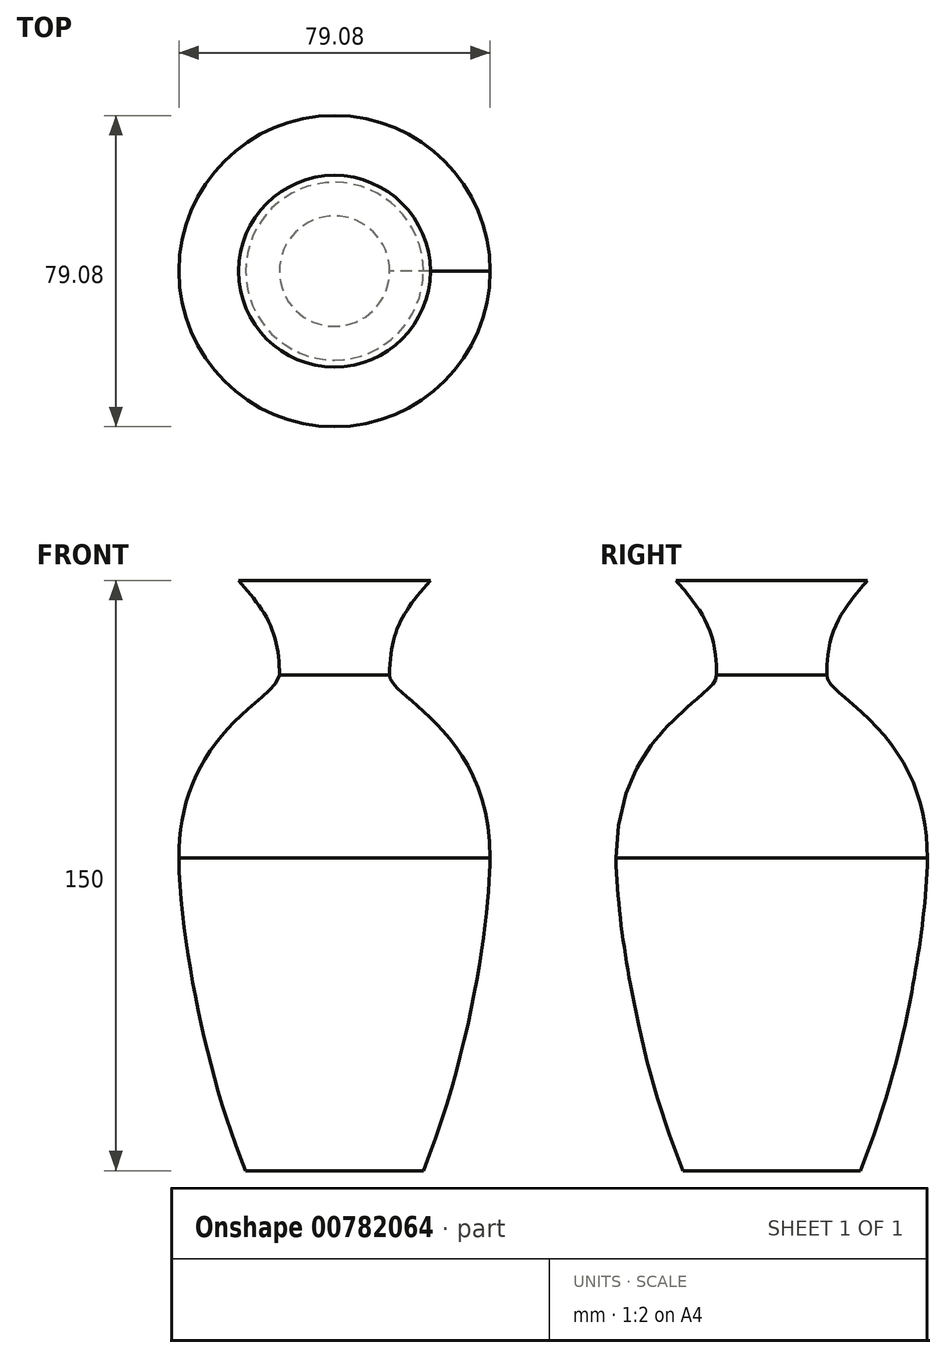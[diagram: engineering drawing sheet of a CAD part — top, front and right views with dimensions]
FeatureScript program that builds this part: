
annotation { "Feature Type Name" : "Feature", "Feature Type Description" : "" }
export const myFeature = defineFeature(function(context is Context, id is Id, definition is map)
    precondition{}
    {
        {
            var Q0;
            Q0=qCreatedBy(makeId("Front.planeOp"),FACE);
            var sketch = newSketch(context, id + "F0", { "sketchPlane" : qUnion([Q0])});
            skLineSegment(sketch, "E0", {"start": v(0, 0) * mm, "end": v(22.56, 0) * mm});
            skFitSpline(sketch, "E1", {"points": [v(22.56, 0) * mm, v(39.54, 79.5) * mm], "startDerivative": vector(38.16, 93.75) * mm, "endDerivative": vector(0, 37.66) * mm});
            skLineSegment(sketch, "E2", {"start": v(22.56, 0) * mm, "end": v(22.56, 175.74) * mm, "construction": true});
            skLineSegment(sketch, "E3", {"start": v(14, 0) * mm, "end": v(14, 181.09) * mm, "construction": true});
            skLineSegment(sketch, "E4", {"start": v(39.54, 0) * mm, "end": v(39.54, 223.58) * mm, "construction": true});
            skFitSpline(sketch, "E5", {"points": [v(39.54, 79.5) * mm, v(14, 125.89) * mm], "startDerivative": vector(0, 96.87) * mm, "endDerivative": vector(0, 17.57) * mm});
            skLineSegment(sketch, "E6", {"start": v(24.33, 0) * mm, "end": v(24.33, 187.13) * mm, "construction": true});
            skFitSpline(sketch, "E7", {"points": [v(14, 125.89) * mm, v(24.33, 150) * mm], "startDerivative": vector(0, 34) * mm, "endDerivative": vector(20.89, 24.41) * mm});
            skLineSegment(sketch, "E8", {"start": v(24.33, 150) * mm, "end": v(0, 150) * mm});
            skLineSegment(sketch, "E9", {"start": v(0, 150) * mm, "end": v(0, 0) * mm});
            skSolve(sketch);
        }
        {
            var Q0;
            Q0=makeQuery(id+"F0.imprint","IMPRINT",FACE,{"disambiguationData":[TD([[makeQuery(id+"F0.imprint","IMPRINT",EDGE,{"derivedFrom":sQuery(id+"F0.wireOp",EDGE,"E0")}),1.0]])]});
            var Q1;
            Q1=sQuery(id+"F0.wireOp",EDGE,"E9");
            revolve(context, id + "F1", {"surfaceOperationType" : NewSurfaceOperationType.NEW, "entities" : qUnion([Q0]), "axis" : qUnion([Q1]), "revolveType" : RevolveType.FULL});
        }
    });
